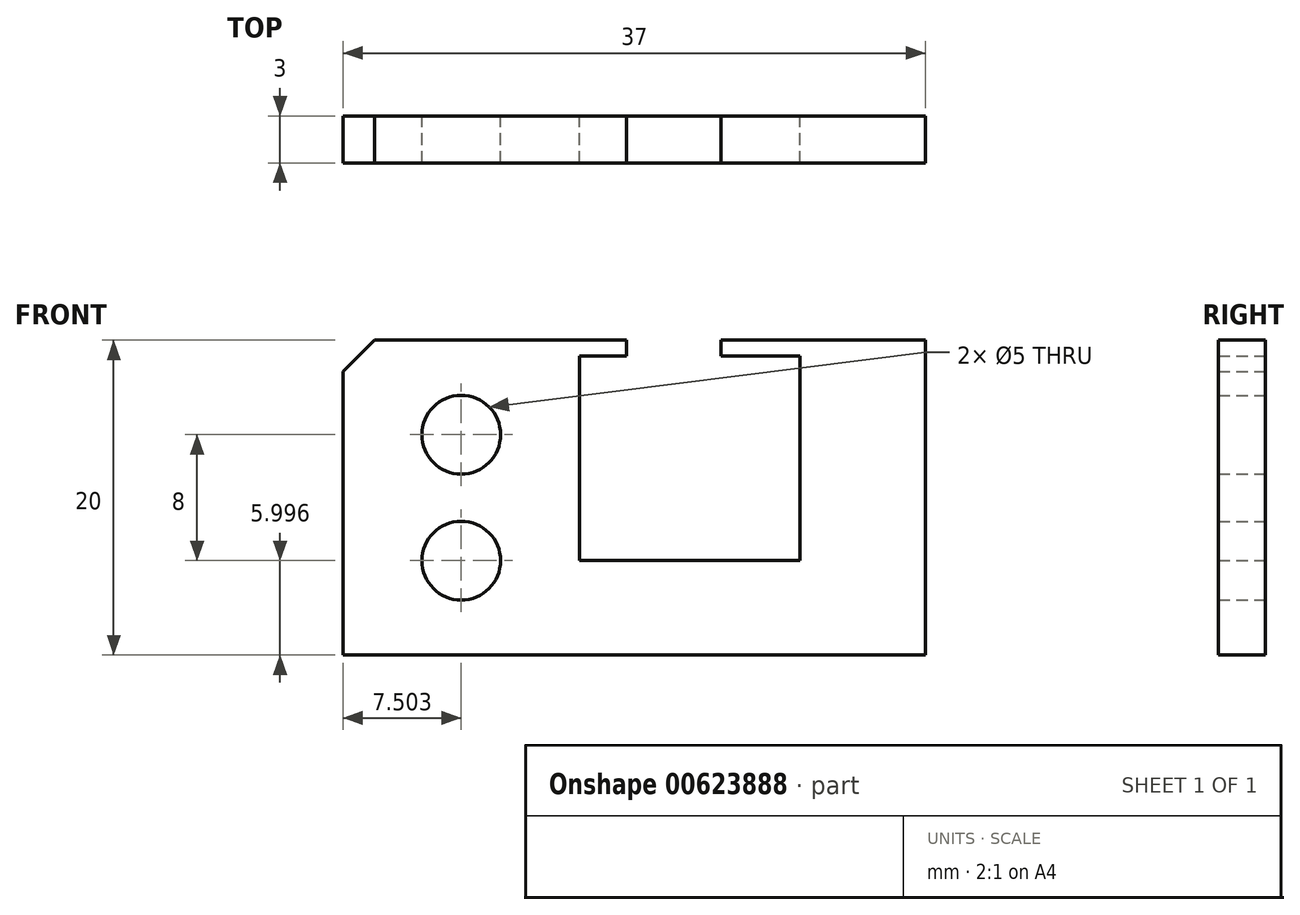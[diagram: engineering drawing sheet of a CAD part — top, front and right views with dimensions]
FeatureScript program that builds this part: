
annotation { "Feature Type Name" : "Feature", "Feature Type Description" : "" }
export const myFeature = defineFeature(function(context is Context, id is Id, definition is map)
    precondition{}
    {
        {
            var Q0;
            Q0=qCreatedBy(makeId("Front.planeOp"),FACE);
            var sketch = newSketch(context, id + "F0", { "sketchPlane" : qUnion([Q0])});
            skLineSegment(sketch, "E0.bottom", {"start": v(-11.1, 12.34) * mm, "end": v(4.9, 12.34) * mm});
            skLineSegment(sketch, "E0.top", {"start": v(-13.1, -7.66) * mm, "end": v(23.9, -7.66) * mm});
            skLineSegment(sketch, "E0.left", {"start": v(-13.1, 10.34) * mm, "end": v(-13.1, -7.66) * mm});
            skLineSegment(sketch, "E0.right", {"start": v(23.9, 12.34) * mm, "end": v(23.9, -7.66) * mm});
            skLineSegment(sketch, "E1", {"start": v(15.9, -1.66) * mm, "end": v(1.9, -1.66) * mm});
            skLineSegment(sketch, "E2", {"start": v(1.9, -1.66) * mm, "end": v(1.9, 11.34) * mm});
            skLineSegment(sketch, "E3", {"start": v(1.9, 11.34) * mm, "end": v(4.9, 11.34) * mm});
            skLineSegment(sketch, "E4", {"start": v(15.9, 11.34) * mm, "end": v(15.9, -1.66) * mm});
            skLineSegment(sketch, "E5", {"start": v(10.9, 12.34) * mm, "end": v(10.9, 11.34) * mm});
            skLineSegment(sketch, "E6", {"start": v(4.9, 12.34) * mm, "end": v(4.9, 11.34) * mm});
            skLineSegment(sketch, "E7.trimOffspring", {"start": v(10.9, 12.34) * mm, "end": v(23.9, 12.34) * mm});
            skLineSegment(sketch, "E8.trimOffspring", {"start": v(10.9, 11.34) * mm, "end": v(15.9, 11.34) * mm});
            skCircle(sketch, "E9", {"center": v(-5.6, -1.66) * mm, "radius": 2.5 * mm});
            skCircle(sketch, "E10", {"center": v(-5.6, 6.34) * mm, "radius": 2.5 * mm});
            skLineSegment(sketch, "E11", {"start": v(-13.1, 10.34) * mm, "end": v(-11.1, 12.34) * mm});
            skPoint(sketch, "E12.orphan", {"position": v(-13.1, 12.34) * mm});
            skSolve(sketch);
        }
        {
            var Q0;
            Q0 = qSketchRegion(id + "F0", true);
            extrude(context, id + "F1", {"entities" : qUnion([Q0]), "depth" : 3 * mm, "offsetDistance" : 25 * mm});
        }
    });
